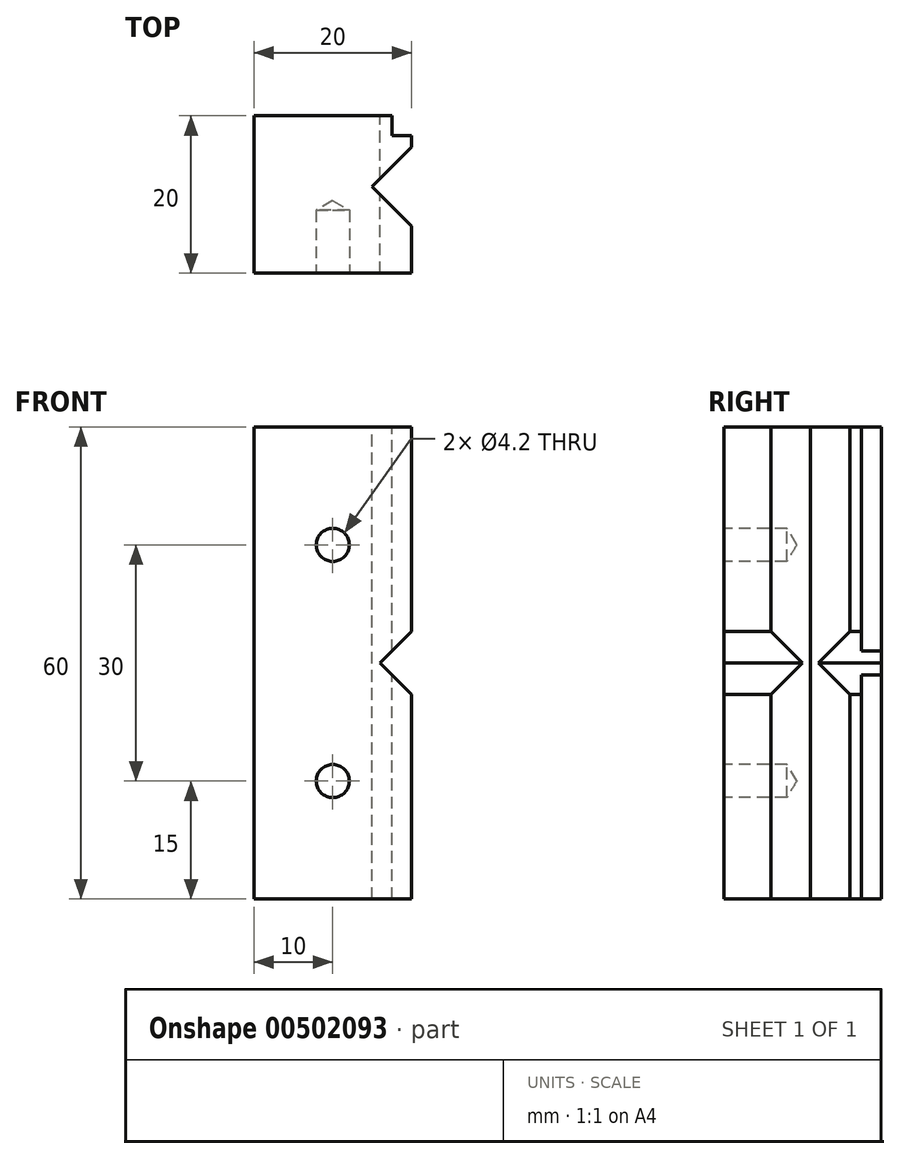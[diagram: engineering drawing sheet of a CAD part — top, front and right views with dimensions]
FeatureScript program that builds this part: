
annotation { "Feature Type Name" : "Feature", "Feature Type Description" : "" }
export const myFeature = defineFeature(function(context is Context, id is Id, definition is map)
    precondition{}
    {
        {
            var Q0;
            Q0=qCreatedBy(makeId("Top.planeOp"),FACE);
            var sketch = newSketch(context, id + "F0", { "sketchPlane" : qUnion([Q0])});
            skLineSegment(sketch, "E0.bottom", {"start": v(0, 0) * mm, "end": v(20, 0) * mm});
            skLineSegment(sketch, "E0.top", {"start": v(0, 20) * mm, "end": v(17.5, 20) * mm});
            skLineSegment(sketch, "E0.left", {"start": v(0, 0) * mm, "end": v(0, 20) * mm});
            skLineSegment(sketch, "E0.right", {"start": v(20, 0) * mm, "end": v(20, 6) * mm});
            skLineSegment(sketch, "E1.top", {"start": v(20, 17.5) * mm, "end": v(17.5, 17.5) * mm});
            skLineSegment(sketch, "E1.right", {"start": v(17.5, 20) * mm, "end": v(17.5, 17.5) * mm});
            skLineSegment(sketch, "E2", {"start": v(20, 16) * mm, "end": v(15, 11) * mm});
            skLineSegment(sketch, "E3", {"start": v(15, 11) * mm, "end": v(20, 6) * mm});
            skLineSegment(sketch, "E4.trimOffspring", {"start": v(20, 16) * mm, "end": v(20, 17.5) * mm});
            skLineSegment(sketch, "E5", {"start": v(15, 11) * mm, "end": v(20.18, 11) * mm, "construction": true});
            skSolve(sketch);
        }
        {
            var Q0;
            Q0=makeQuery(id+"F0.imprint","IMPRINT",FACE,{"disambiguationData":[TD([[makeQuery(id+"F0.imprint","IMPRINT",EDGE,{"derivedFrom":sQuery(id+"F0.wireOp",EDGE,"E0.bottom")}),1.0]])]});
            extrude(context, id + "F1", {"entities" : qUnion([Q0]), "oppositeDirection" : true, "depth" : 60 * mm, "offsetDistance" : 25 * mm});
        }
        {
            var Q0;
            Q0=makeQuery(id+"F1.opExtrude","SWEPT_FACE",FACE,{"disambiguationData":[OSD([sQuery(id+"F0.wireOp",EDGE,"E0.top")])]});
            var sketch = newSketch(context, id + "F2", { "sketchPlane" : qUnion([Q0])});
            skLineSegment(sketch, "E6", {"start": v(-21.12, -24.88) * mm, "end": v(-16, -30) * mm});
            skLineSegment(sketch, "E7", {"start": v(-16, -30) * mm, "end": v(-21.12, -35.12) * mm});
            skLineSegment(sketch, "E8", {"start": v(-21.12, -35.12) * mm, "end": v(-21.12, -24.88) * mm});
            skLineSegment(sketch, "E9", {"start": v(-16, -30) * mm, "end": v(4.7, -30) * mm, "construction": true});
            skSolve(sketch);
        }
        {
            var Q0;
            {var subQ0=sQuery(id+"F2.wireOp",EDGE,"E8");Q0=makeQuery(id+"F2.imprint","IMPRINT",FACE,{"disambiguationData":[TD([[makeQuery(id+"F2.imprint","IMPRINT",EDGE,{"derivedFrom":subQ0}),-1.0]])]});}
            var Q1;
            {var subQ0=sQuery(id+"F2.wireOp",EDGE,"E7");var subQ1=sQuery(id+"F2.wireOp",EDGE,"E6");var subQ2=makeQuery(id+"F2.imprint","INTERSECT",VERTEX,{"derivedFrom":[subQ1,subQ0]});Q1=makeQuery(id+"F2.imprint","IMPRINT",FACE,{"disambiguationData":[TD([[makeQuery(id+"F2.imprint","IMPRINT",EDGE,{"disambiguationData":[TD([[subQ2,1.0]])],"derivedFrom":subQ1}),-1.0]])]});}
            extrude(context, id + "F3", {"entities" : qUnion([Q0, Q1]), "operationType" : NewBodyOperationType.REMOVE, "oppositeDirection" : true, "depth" : 25 * mm, "offsetDistance" : 25 * mm});
        }
        {
            var Q0;
            Q0=makeQuery(id+"F1.opExtrude","SWEPT_FACE",FACE,{"disambiguationData":[OSD([sQuery(id+"F0.wireOp",EDGE,"E0.bottom")])]});
            var sketch = newSketch(context, id + "F4", { "sketchPlane" : qUnion([Q0])});
            skPoint(sketch, "E10", {"position": v(10, -15) * mm});
            skPoint(sketch, "E10.positionSnap0", {"position": v(10, 0) * mm});
            skPoint(sketch, "E11", {"position": v(10, -45) * mm});
            skSolve(sketch);
        }
        {
            var Q0;
            Q0=sQuery(id+"F4.wireOp",VERTEX,"E10");
            var Q1;
            Q1=sQuery(id+"F4.wireOp",VERTEX,"E11");
            var Q2;
            Q2=makeQuery(id+"F1.opExtrude","SWEPT_BODY",BODY,{"disambiguationData":[OSD([sQuery(id+"F0.wireOp",EDGE,"E0.bottom"),sQuery(id+"F0.wireOp",EDGE,"E0.top"),sQuery(id+"F0.wireOp",EDGE,"E0.left"),sQuery(id+"F0.wireOp",EDGE,"E0.right"),sQuery(id+"F0.wireOp",EDGE,"E1.top"),sQuery(id+"F0.wireOp",EDGE,"E1.right"),sQuery(id+"F0.wireOp",EDGE,"E2"),sQuery(id+"F0.wireOp",EDGE,"E3"),sQuery(id+"F0.wireOp",EDGE,"E4.trimOffspring")])]});
            hole(context, id + "F5", {"style" : HoleStyle.SIMPLE, "endStyle" : HoleEndStyle.BLIND, "standardTappedOrClearance" : lookupTablePath({ "standard" : "ISO", "engagement" : "75%", "pitch" : "0.8 mm", "size" : "M5", "type" : "Tapped" }), "standardBlindInLast" : lookupTablePath({ "standard" : "ISO", "fit" : "Normal", "engagement" : "75%", "pitch" : "0.8 mm", "size" : "M5", "type" : "Clearance & tapped" }), "holeDiameter" : 4.2 * mm, "majorDiameter" : 5 * mm, "showTappedDepth" : true, "holeDepth" : 8 * mm, "isTappedThrough" : true, "tappedDepth" : 6 * mm, "tapClearance" : 2.5, "locations" : qUnion([Q0, Q1]), "scope" : qUnion([Q2])});
        }
    });
